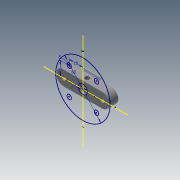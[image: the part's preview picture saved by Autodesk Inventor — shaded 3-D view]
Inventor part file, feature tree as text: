
AUTODESK INVENTOR PART (.ipt)
format: ipt  version: 2015 (Build 190159000, 159)  size: 123,904 bytes
history: native  units: mm
features: other x3, sketch x3, extrude x2, plane x1
ambient origin geometry x8: Origin, YZ Plane, XZ Plane, XY Plane, X Axis, Y Axis, Z Axis, Center Point
bodies: Body1 (feature_tree)
feature tree (9):
  other  "Blocks"
  sketch  "Sketch1"  dims[d0=60.0mm d1=20.0mm]
  plane  "Work Plane1"
  extrude  "Extrusion4"  Depth=20.0mm
  extrude  "Extrusion5"  Depth=10.0mm
  other  "Block1"
  other  "Block2"
  sketch  "Sketch6"  dims[d7=10.0mm d8=40.0mm]
  sketch  "Sketch7"  dims[d31=5.0mm d32=15.0mm d33=15.0mm d36=8.0mm d37=5.0mm d38=5.0mm d39=42.426407mm d40=10.0mm d41=10.0mm d42=0.0mm d43=5.0mm d44=5.0mm d45=21.213203mm d46=10.0mm d47=0.0mm]
